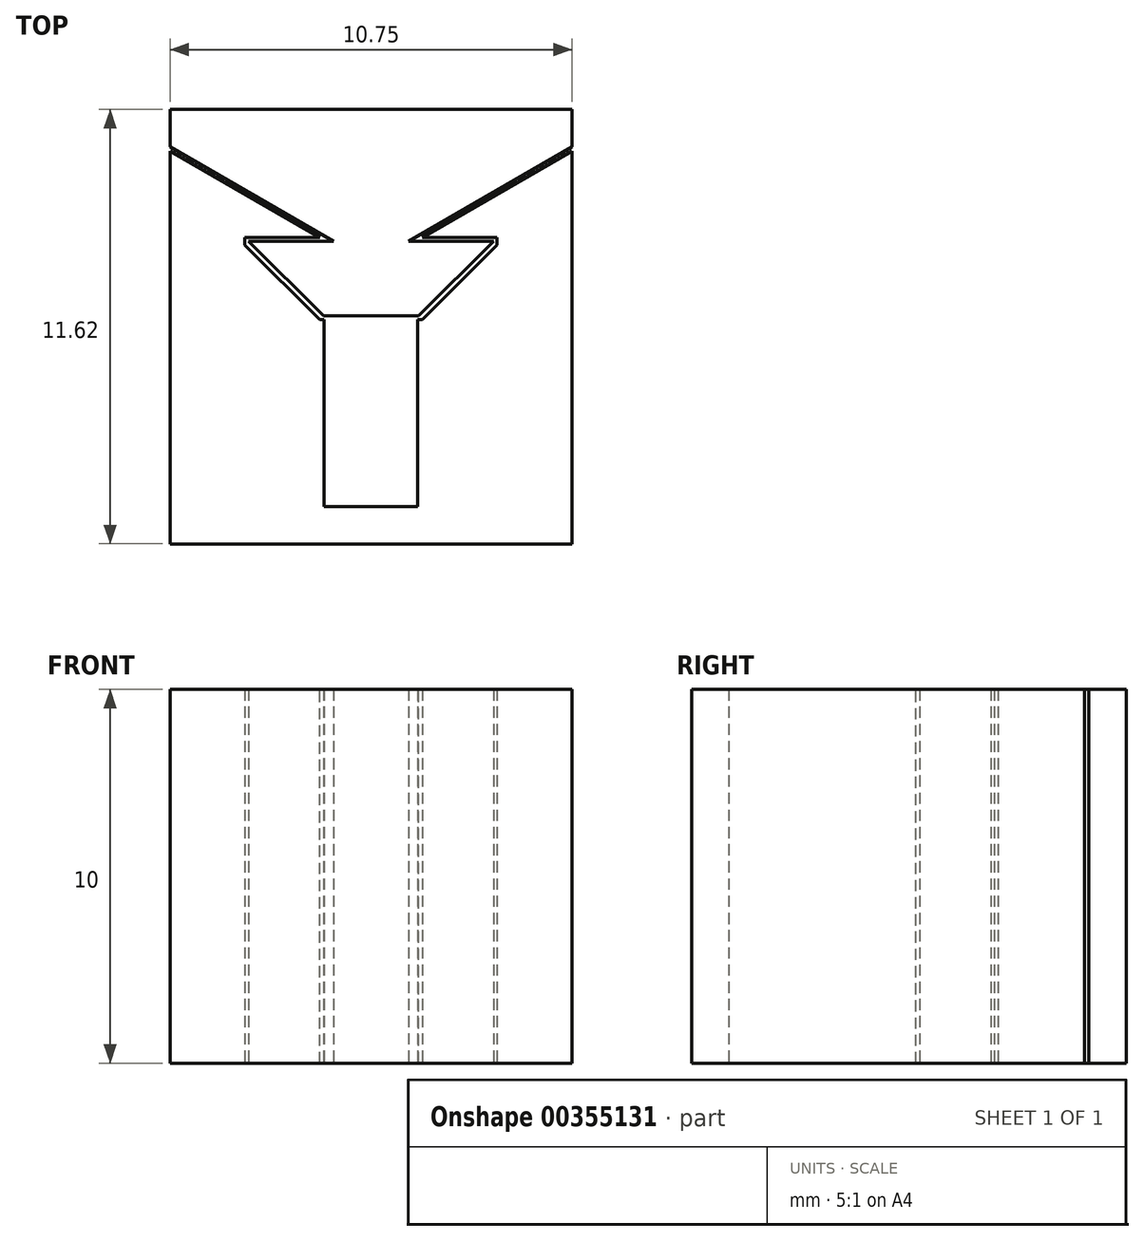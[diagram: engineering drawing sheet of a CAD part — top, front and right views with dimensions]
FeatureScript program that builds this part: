
annotation { "Feature Type Name" : "Feature", "Feature Type Description" : "" }
export const myFeature = defineFeature(function(context is Context, id is Id, definition is map)
    precondition{}
    {
        {
            var Q0;
            Q0=qCreatedBy(makeId("Top.planeOp"),FACE);
            var sketch = newSketch(context, id + "F0", { "sketchPlane" : qUnion([Q0])});
            skLineSegment(sketch, "E0.top", {"start": v(-3.84, -9.3) * mm, "end": v(6.9, -9.3) * mm});
            skLineSegment(sketch, "E0.left", {"start": v(-3.84, -3.3) * mm, "end": v(-3.84, -9.3) * mm});
            skLineSegment(sketch, "E0.right", {"start": v(6.9, -3.3) * mm, "end": v(6.9, -9.3) * mm});
            skLineSegment(sketch, "E1", {"start": v(6.9, -3.3) * mm, "end": v(2.79, -3.3) * mm});
            skLineSegment(sketch, "E2", {"start": v(2.79, -3.3) * mm, "end": v(2.79, -8.3) * mm});
            skLineSegment(sketch, "E3", {"start": v(2.79, -8.3) * mm, "end": v(0.29, -8.3) * mm});
            skLineSegment(sketch, "E4", {"start": v(0.29, -8.3) * mm, "end": v(0.29, -3.3) * mm});
            skLineSegment(sketch, "E5", {"start": v(0.29, -3.3) * mm, "end": v(-3.84, -3.3) * mm});
            skLineSegment(sketch, "E6", {"start": v(6.9, -3.3) * mm, "end": v(6.9, 1.2) * mm});
            skLineSegment(sketch, "E7", {"start": v(6.9, 1.2) * mm, "end": v(2.9, -1.1) * mm});
            skLineSegment(sketch, "E8", {"start": v(2.9, -1.1) * mm, "end": v(4.9, -1.1) * mm});
            skLineSegment(sketch, "E9", {"start": v(4.9, -1.1) * mm, "end": v(4.9, -3.3) * mm});
            skLineSegment(sketch, "E10", {"start": v(1.54, -9.3) * mm, "end": v(1.54, 0.07) * mm, "construction": true});
            skPoint(sketch, "E10.endSnap0", {"position": v(1.54, -8.3) * mm});
            skLineSegment(sketch, "E11.MirrorCS", {"start": v(-3.84, 1.2) * mm, "end": v(0.16, -1.1) * mm});
            skLineSegment(sketch, "E12.MirrorCS", {"start": v(-3.84, -3.3) * mm, "end": v(-3.84, 1.2) * mm});
            skLineSegment(sketch, "E13.MirrorCS", {"start": v(-1.84, -1.1) * mm, "end": v(-1.84, -3.3) * mm});
            skLineSegment(sketch, "E14.MirrorCS", {"start": v(0.16, -1.1) * mm, "end": v(-1.84, -1.1) * mm});
            skLineSegment(sketch, "E15", {"start": v(4.8, -1.2) * mm, "end": v(2.54, -1.2) * mm});
            skLineSegment(sketch, "E16", {"start": v(2.54, -1.2) * mm, "end": v(6.9, 1.32) * mm});
            skLineSegment(sketch, "E17", {"start": v(6.9, 1.32) * mm, "end": v(6.9, 2.32) * mm});
            skLineSegment(sketch, "E18", {"start": v(6.9, 2.32) * mm, "end": v(1.54, 2.32) * mm});
            skLineSegment(sketch, "E19", {"start": v(4.8, -1.2) * mm, "end": v(4.8, -3.2) * mm});
            skLineSegment(sketch, "E20", {"start": v(4.8, -3.2) * mm, "end": v(1.54, -3.2) * mm});
            skLineSegment(sketch, "E21.MirrorCS", {"start": v(-3.84, 2.32) * mm, "end": v(1.54, 2.32) * mm});
            skLineSegment(sketch, "E22.MirrorCS", {"start": v(-3.84, 1.32) * mm, "end": v(-3.84, 2.32) * mm});
            skLineSegment(sketch, "E23.MirrorCS", {"start": v(0.54, -1.2) * mm, "end": v(-3.84, 1.32) * mm});
            skLineSegment(sketch, "E24.MirrorCS", {"start": v(-1.74, -3.2) * mm, "end": v(1.54, -3.2) * mm});
            skLineSegment(sketch, "E25.MirrorCS", {"start": v(-1.74, -1.2) * mm, "end": v(0.54, -1.2) * mm});
            skLineSegment(sketch, "E26.MirrorCS", {"start": v(-1.74, -1.2) * mm, "end": v(-1.74, -3.2) * mm});
            skSolve(sketch);
        }
        {
            var Q0;
            Q0=makeQuery(id+"F0.imprint","IMPRINT",FACE,{"disambiguationData":[TD([[makeQuery(id+"F0.imprint","IMPRINT",EDGE,{"derivedFrom":sQuery(id+"F0.wireOp",EDGE,"E0.top")}),1.0]])]});
            var Q1;
            {var subQ0=sQuery(id+"F0.wireOp",EDGE,"E6");Q1=makeQuery(id+"F0.imprint","IMPRINT",FACE,{"disambiguationData":[TD([[makeQuery(id+"F0.imprint","IMPRINT",EDGE,{"derivedFrom":subQ0}),1.0]])]});}
            var Q2;
            Q2=makeQuery(id+"F0.imprint","IMPRINT",FACE,{"disambiguationData":[TD([[makeQuery(id+"F0.imprint","IMPRINT",EDGE,{"derivedFrom":sQuery(id+"F0.wireOp",EDGE,"E11.MirrorCS")}),-1.0]])]});
            var Q3;
            Q3=makeQuery(id+"F0.imprint","IMPRINT",FACE,{"disambiguationData":[TD([[makeQuery(id+"F0.imprint","IMPRINT",EDGE,{"derivedFrom":sQuery(id+"F0.wireOp",EDGE,"E15")}),1.0]])]});
            var Q4;
            {var subQ0=sQuery(id+"F0.wireOp",EDGE,"E24.MirrorCS");var subQ1=sQuery(id+"F0.wireOp",EDGE,"E20");var subQ2=makeQuery(id+"F0.imprint","INTERSECT",VERTEX,{"derivedFrom":[subQ1,subQ0]});Q4=makeQuery(id+"F0.imprint","IMPRINT",FACE,{"disambiguationData":[TD([[makeQuery(id+"F0.imprint","IMPRINT",EDGE,{"disambiguationData":[TD([[subQ2,1.0]])],"derivedFrom":subQ1}),-1.0]])]});}
            extrude(context, id + "F1", {"entities" : qUnion([Q0, Q1, Q2, Q3, Q4]), "endBound" : BoundingType.SYMMETRIC, "depth" : 10 * mm});
        }
        {
            var Q0;
            Q0=makeQuery(id+"F1.opExtrude","SWEPT_EDGE",EDGE,{"disambiguationData":[OSD([sQuery(id+"F0.wireOp",EDGE,"E1"),sQuery(id+"F0.wireOp",EDGE,"E9")])]});
            var Q1;
            Q1=makeQuery(id+"F1.opExtrude","SWEPT_EDGE",EDGE,{"disambiguationData":[OSD([sQuery(id+"F0.wireOp",EDGE,"E5"),sQuery(id+"F0.wireOp",EDGE,"E13.MirrorCS")])]});
            var Q2;
            Q2=makeQuery(id+"F1.opExtrude","SWEPT_EDGE",EDGE,{"disambiguationData":[OSD([sQuery(id+"F0.wireOp",EDGE,"E19"),sQuery(id+"F0.wireOp",EDGE,"E20")])]});
            var Q3;
            Q3=makeQuery(id+"F1.opExtrude","SWEPT_EDGE",EDGE,{"disambiguationData":[OSD([sQuery(id+"F0.wireOp",EDGE,"E24.MirrorCS"),sQuery(id+"F0.wireOp",EDGE,"E26.MirrorCS")])]});
            chamfer(context, id + "F2", {"entities" : qUnion([Q0, Q1, Q2, Q3]), "width" : 2 * mm, "tangentPropagation" : true});
        }
    });
